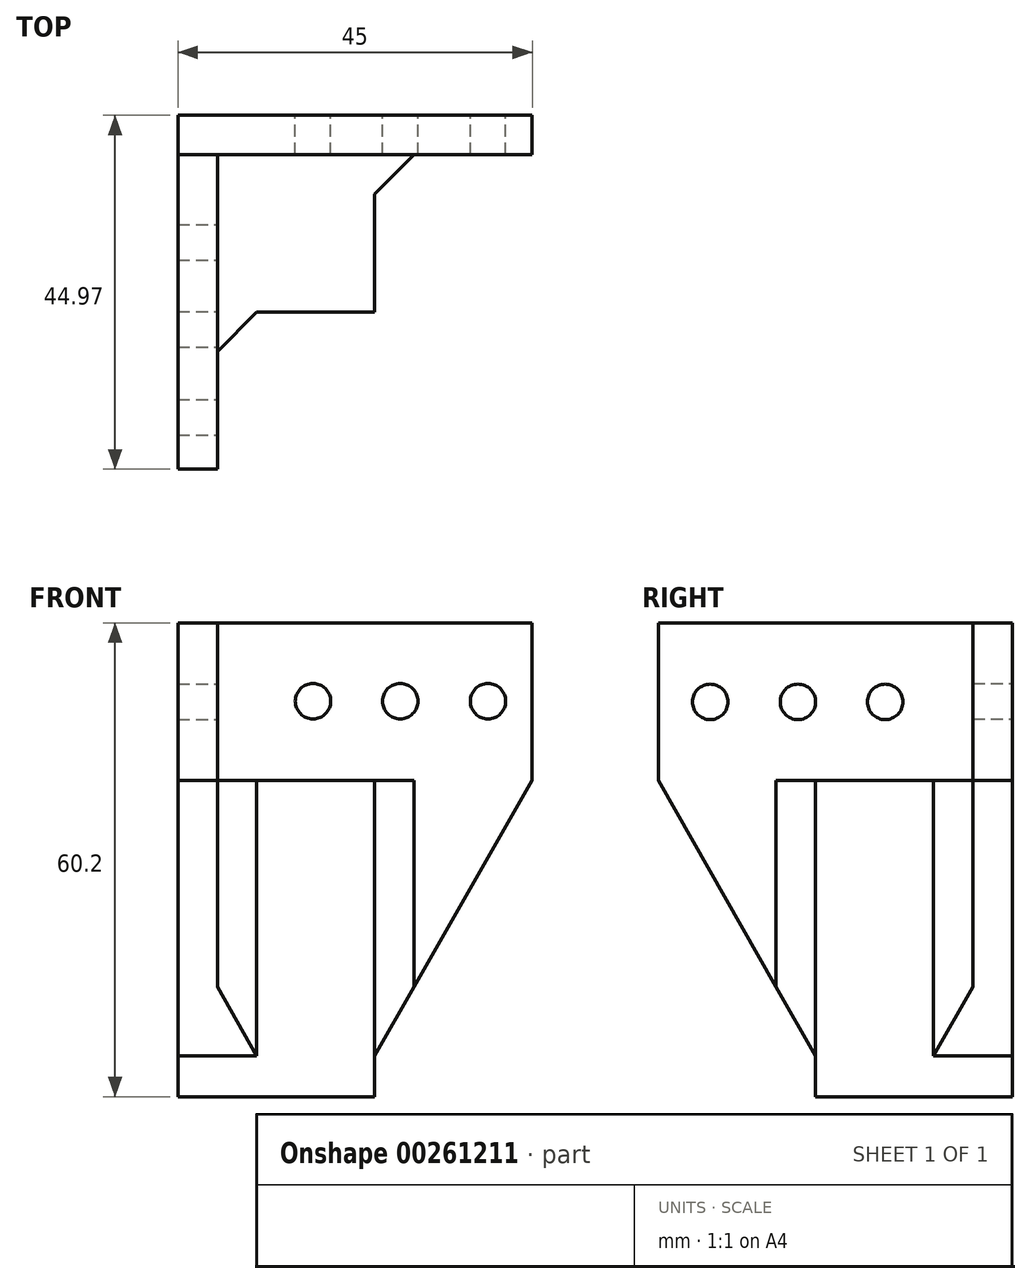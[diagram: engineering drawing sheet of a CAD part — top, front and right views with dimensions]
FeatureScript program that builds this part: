
annotation { "Feature Type Name" : "Feature", "Feature Type Description" : "" }
export const myFeature = defineFeature(function(context is Context, id is Id, definition is map)
    precondition{}
    {
        {
            var Q0;
            Q0=qCreatedBy(makeId("Front.planeOp"),FACE);
            var sketch = newSketch(context, id + "F0", { "sketchPlane" : qUnion([Q0])});
            skLineSegment(sketch, "E0.bottom", {"start": v(-60.77, 44.74) * mm, "end": v(-20.77, 44.74) * mm});
            skLineSegment(sketch, "E0.top", {"start": v(-60.77, -10.26) * mm, "end": v(-40.77, -10.26) * mm});
            skLineSegment(sketch, "E0.left", {"start": v(-60.77, 44.74) * mm, "end": v(-60.77, -10.26) * mm});
            skLineSegment(sketch, "E0.right", {"start": v(-20.77, 44.74) * mm, "end": v(-20.77, 24.74) * mm});
            skLineSegment(sketch, "E1.top", {"start": v(-60.77, 24.74) * mm, "end": v(-20.77, 24.74) * mm, "construction": true});
            skLineSegment(sketch, "E1.left", {"start": v(-60.77, 44.74) * mm, "end": v(-60.77, 24.74) * mm});
            skLineSegment(sketch, "E2", {"start": v(-60.77, 34.74) * mm, "end": v(-20.77, 34.74) * mm, "construction": true});
            skLineSegment(sketch, "E3", {"start": v(-40.77, 44.74) * mm, "end": v(-40.77, 24.74) * mm, "construction": true});
            skLineSegment(sketch, "E4", {"start": v(-20.77, 24.74) * mm, "end": v(-40.77, -10.26) * mm});
            skPoint(sketch, "E5.orphan", {"position": v(-20.77, -10.26) * mm});
            skCircle(sketch, "E6", {"center": v(-26.39, 34.78) * mm, "radius": 2.25 * mm});
            skCircle(sketch, "E7", {"center": v(-37.54, 34.78) * mm, "radius": 2.25 * mm});
            skPoint(sketch, "E8.center.orphan", {"position": v(-39.79, 34.78) * mm});
            skCircle(sketch, "E9", {"center": v(-48.62, 34.78) * mm, "radius": 2.25 * mm});
            skPoint(sketch, "E10.center.orphan", {"position": v(-40.77, 34.74) * mm});
            skSolve(sketch);
        }
        {
            var Q0;
            Q0=makeQuery(id+"F0.imprint","IMPRINT",FACE,{"disambiguationData":[TD([[makeQuery(id+"F0.imprint","IMPRINT",EDGE,{"derivedFrom":sQuery(id+"F0.wireOp",EDGE,"E0.top")}),1.0]])]});
            extrude(context, id + "F1", {"entities" : qUnion([Q0]), "depth" : 5 * mm});
        }
        {
            var Q0;
            Q0=makeQuery(id+"F1.opExtrude","SWEPT_FACE",FACE,{"disambiguationData":[OSD([sQuery(id+"F0.wireOp",EDGE,"E0.left"),sQuery(id+"F0.wireOp",EDGE,"E1.left")])]});
            var sketch = newSketch(context, id + "F2", { "sketchPlane" : qUnion([Q0])});
            skLineSegment(sketch, "E11.bottom", {"start": v(4.97, 44.69) * mm, "end": v(44.97, 44.69) * mm});
            skLineSegment(sketch, "E11.top", {"start": v(4.97, -10.31) * mm, "end": v(24.97, -10.31) * mm});
            skLineSegment(sketch, "E11.left", {"start": v(4.97, 44.69) * mm, "end": v(4.97, -10.31) * mm});
            skLineSegment(sketch, "E11.right", {"start": v(44.97, 44.69) * mm, "end": v(44.97, 24.69) * mm});
            skLineSegment(sketch, "E12.top", {"start": v(4.97, 24.69) * mm, "end": v(44.97, 24.69) * mm, "construction": true});
            skLineSegment(sketch, "E12.left", {"start": v(4.97, 44.69) * mm, "end": v(4.97, 24.69) * mm});
            skLineSegment(sketch, "E13", {"start": v(4.97, 34.69) * mm, "end": v(44.97, 34.69) * mm, "construction": true});
            skCircle(sketch, "E14", {"center": v(38.37, 34.69) * mm, "radius": 2.25 * mm});
            skLineSegment(sketch, "E15", {"start": v(24.97, 44.69) * mm, "end": v(24.97, 24.69) * mm, "construction": true});
            skLineSegment(sketch, "E16", {"start": v(44.97, 24.69) * mm, "end": v(24.97, -10.31) * mm});
            skPoint(sketch, "E17.orphan", {"position": v(44.97, -10.31) * mm});
            skCircle(sketch, "E18", {"center": v(27.22, 34.69) * mm, "radius": 2.25 * mm});
            skPoint(sketch, "E19.center.orphan", {"position": v(24.97, 34.69) * mm});
            skCircle(sketch, "E20", {"center": v(16.14, 34.69) * mm, "radius": 2.25 * mm});
            skSolve(sketch);
        }
        {
            var Q0;
            Q0=makeQuery(id+"F2.imprint","IMPRINT",FACE,{"disambiguationData":[TD([[makeQuery(id+"F2.imprint","IMPRINT",EDGE,{"derivedFrom":sQuery(id+"F2.wireOp",EDGE,"E11.top")}),1.0]])]});
            extrude(context, id + "F3", {"entities" : qUnion([Q0]), "depth" : 5 * mm});
        }
        {
            var Q0;
            Q0=makeQuery(id+"F1.opExtrude","SWEPT_FACE",FACE,{"disambiguationData":[OSD([sQuery(id+"F0.wireOp",EDGE,"E0.left"),sQuery(id+"F0.wireOp",EDGE,"E1.left")])]});
            var sketch = newSketch(context, id + "F4", { "sketchPlane" : qUnion([Q0])});
            skLineSegment(sketch, "E21.bottom", {"start": v(0, 44.74) * mm, "end": v(5, 44.74) * mm});
            skLineSegment(sketch, "E21.top", {"start": v(0, -10.26) * mm, "end": v(5, -10.26) * mm});
            skLineSegment(sketch, "E21.left", {"start": v(0, 44.74) * mm, "end": v(0, -10.26) * mm});
            skLineSegment(sketch, "E21.right", {"start": v(5, 44.74) * mm, "end": v(5, -10.26) * mm});
            skSolve(sketch);
        }
        {
            var Q0;
            Q0=qSketchRegion(id+"F4",true);
            extrude(context, id + "F5", {"entities" : qUnion([Q0]), "operationType" : NewBodyOperationType.ADD, "depth" : 5 * mm});
        }
        {
            var Q0;
            Q0=makeQuery(id+"F5.boolean.opBoolean","MERGE",FACE,{"derivedFrom":[makeQuery(id+"F1.opExtrude","SWEPT_FACE",FACE,{"disambiguationData":[OSD([sQuery(id+"F0.wireOp",EDGE,"E0.top")])]}),makeQuery(id+"F5.opExtrude","SWEPT_FACE",FACE,{"disambiguationData":[OSD([sQuery(id+"F4.wireOp",EDGE,"E21.top")])]})]});
            var sketch = newSketch(context, id + "F6", { "sketchPlane" : qUnion([Q0])});
            skLineSegment(sketch, "E22.bottom", {"start": v(-65.77, 0) * mm, "end": v(-40.77, 0) * mm});
            skLineSegment(sketch, "E22.top", {"start": v(-65.77, 25) * mm, "end": v(-40.77, 25) * mm});
            skLineSegment(sketch, "E22.left", {"start": v(-65.77, 0) * mm, "end": v(-65.77, 25) * mm});
            skLineSegment(sketch, "E22.right", {"start": v(-40.77, 0) * mm, "end": v(-40.77, 25) * mm});
            skSolve(sketch);
        }
        {
            var Q0;
            Q0=qSketchRegion(id+"F6",true);
            extrude(context, id + "F7", {"entities" : qUnion([Q0]), "operationType" : NewBodyOperationType.ADD, "depth" : 5.2 * mm, "hasSecondDirection" : true, "secondDirectionOppositeDirection" : true, "secondDirectionDepth" : 35 * mm});
        }
        {
            var Q0;
            Q0=makeQuery(id+"F7.boolean.opBoolean","INTERSECT",EDGE,{"derivedFrom":[makeQuery(id+"F5.boolean.opBoolean","MERGE",FACE,{"derivedFrom":[makeQuery(id+"F3.opExtrude","CAP_FACE",FACE,{"disambiguationData":[OSD([sQuery(id+"F0.wireOp",EDGE,"E0.top"),sQuery(id+"F0.wireOp",EDGE,"E0.left"),sQuery(id+"F0.wireOp",EDGE,"E1.left"),sQuery(id+"F2.wireOp",EDGE,"E11.top"),sQuery(id+"F2.wireOp",EDGE,"E11.left"),sQuery(id+"F2.wireOp",EDGE,"E11.bottom"),sQuery(id+"F2.wireOp",EDGE,"E11.right"),sQuery(id+"F2.wireOp",EDGE,"E14"),sQuery(id+"F2.wireOp",EDGE,"E16"),sQuery(id+"F2.wireOp",EDGE,"E18"),sQuery(id+"F2.wireOp",EDGE,"E20")])],"isStart":true}),makeQuery(id+"F5.opExtrude","CAP_FACE",FACE,{"disambiguationData":[OSD([sQuery(id+"F4.wireOp",EDGE,"E21.bottom"),sQuery(id+"F4.wireOp",EDGE,"E21.top"),sQuery(id+"F4.wireOp",EDGE,"E21.left"),sQuery(id+"F4.wireOp",EDGE,"E21.right")])],"isStart":true})]}),makeQuery(id+"F7.opExtrude","SWEPT_FACE",FACE,{"disambiguationData":[OSD([sQuery(id+"F6.wireOp",EDGE,"E22.top")])]})]});
            var Q1;
            Q1=makeQuery(id+"F7.boolean.opBoolean","INTERSECT",EDGE,{"derivedFrom":[makeQuery(id+"F5.boolean.opBoolean","MERGE",FACE,{"derivedFrom":[makeQuery(id+"F1.opExtrude","CAP_FACE",FACE,{"disambiguationData":[OSD([sQuery(id+"F0.wireOp",EDGE,"E0.top"),sQuery(id+"F0.wireOp",EDGE,"E0.left"),sQuery(id+"F0.wireOp",EDGE,"E0.bottom"),sQuery(id+"F0.wireOp",EDGE,"E1.left"),sQuery(id+"F0.wireOp",EDGE,"E0.right"),sQuery(id+"F0.wireOp",EDGE,"E4"),sQuery(id+"F0.wireOp",EDGE,"E6"),sQuery(id+"F0.wireOp",EDGE,"E7"),sQuery(id+"F0.wireOp",EDGE,"E9")])],"isStart":false}),makeQuery(id+"F5.opExtrude","SWEPT_FACE",FACE,{"disambiguationData":[OSD([sQuery(id+"F4.wireOp",EDGE,"E21.right")])]})]}),makeQuery(id+"F7.opExtrude","SWEPT_FACE",FACE,{"disambiguationData":[OSD([sQuery(id+"F6.wireOp",EDGE,"E22.right")])]})]});
            chamfer(context, id + "F8", {"entities" : qUnion([Q0, Q1]), "width" : 5 * mm, "tangentPropagation" : true});
        }
    });
